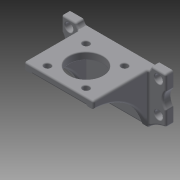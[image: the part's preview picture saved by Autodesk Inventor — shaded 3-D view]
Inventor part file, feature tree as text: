
AUTODESK INVENTOR PART (.ipt)
format: ipt  version: 2014 (Build 180170000, 170)  size: 432,128 bytes
history: native  units: in
note: dims shown in document units (in); Inventor stores cm internally (conversion verified against a paired STEP export)
features: extrude x4, fillet x4, sketch x4, mirror x1
ambient origin geometry x8: Origin, YZ Plane, XZ Plane, XY Plane, X Axis, Y Axis, Z Axis, Center Point
bodies: Solid1 (feature_tree)
feature tree (13):
  extrude  "Extrusion1"  Depth=1.1024in
  extrude  "Extrusion2"  Depth=0.248in
  extrude  "Extrusion4"  Depth=0.315in
  mirror  "Mirror1"
  extrude  "Extrusion5"  Depth=0.0591in
  fillet  "Fillet1"  Radius=0.4724in
  fillet  "Fillet2"  Radius=0.3937in
  fillet  "Fillet3"  Radius=0.9843in
  fillet  "Fillet4"  Radius=0.1969in
  sketch  "Sketch1"  dims[d0=2.2047in d1=1.1024in]
  sketch  "Sketch2"  dims[d2=1.5748in d3=0.248in]
  sketch  "Sketch3"  dims[d4=0.315in d5=0.315in]
  sketch  "Sketch4"  dims[d6=0.4921in d7=0.9843in d8=0.4724in d9=0.3937in d10=0.9843in d11=0.1969in d12=0.2362in d13=0.0in d14=0.2362in d15=1.7323in d16=0.0in d17=1.8898in d20=0.2362in d21=0.0in d22=0.1969in d23=1.2205in d24=1.2205in d25=1.063in d26=0.2362in d27=0.0in d28=0.0295in d29=0.0591in d30=0.0591in d31=0.0591in]
